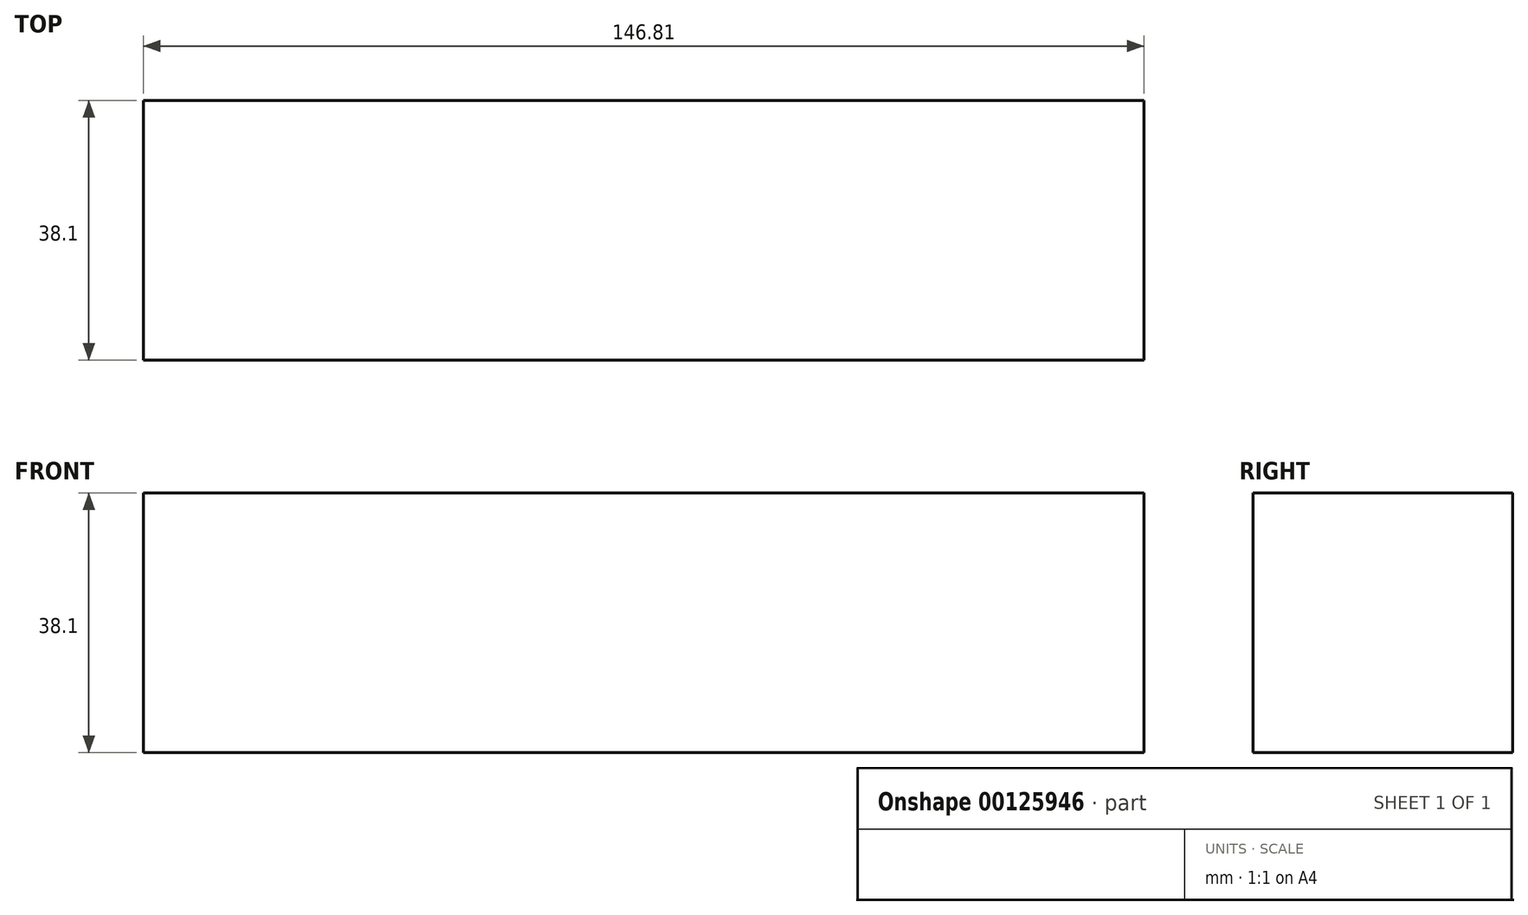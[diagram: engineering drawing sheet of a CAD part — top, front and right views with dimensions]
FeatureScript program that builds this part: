
annotation { "Feature Type Name" : "Feature", "Feature Type Description" : "" }
export const myFeature = defineFeature(function(context is Context, id is Id, definition is map)
    precondition{}
    {
        {
            var Q0;
            Q0=qCreatedBy(makeId("Top.planeOp"),FACE);
            var sketch = newSketch(context, id + "F0", { "sketchPlane" : qUnion([Q0])});
            skLineSegment(sketch, "E0.bottom", {"start": v(0, 0) * mm, "end": v(-146.81, 0) * mm});
            skLineSegment(sketch, "E0.top", {"start": v(0, -38.1) * mm, "end": v(-146.81, -38.1) * mm});
            skLineSegment(sketch, "E0.left", {"start": v(0, 0) * mm, "end": v(0, -38.1) * mm});
            skLineSegment(sketch, "E0.right", {"start": v(-146.81, 0) * mm, "end": v(-146.81, -38.1) * mm});
            skSolve(sketch);
        }
        {
            var Q0;
            Q0 = qSketchRegion(id + "F0", true);
            extrude(context, id + "F1", {"entities" : qUnion([Q0]), "depth" : 38.1 * mm});
        }
    });
